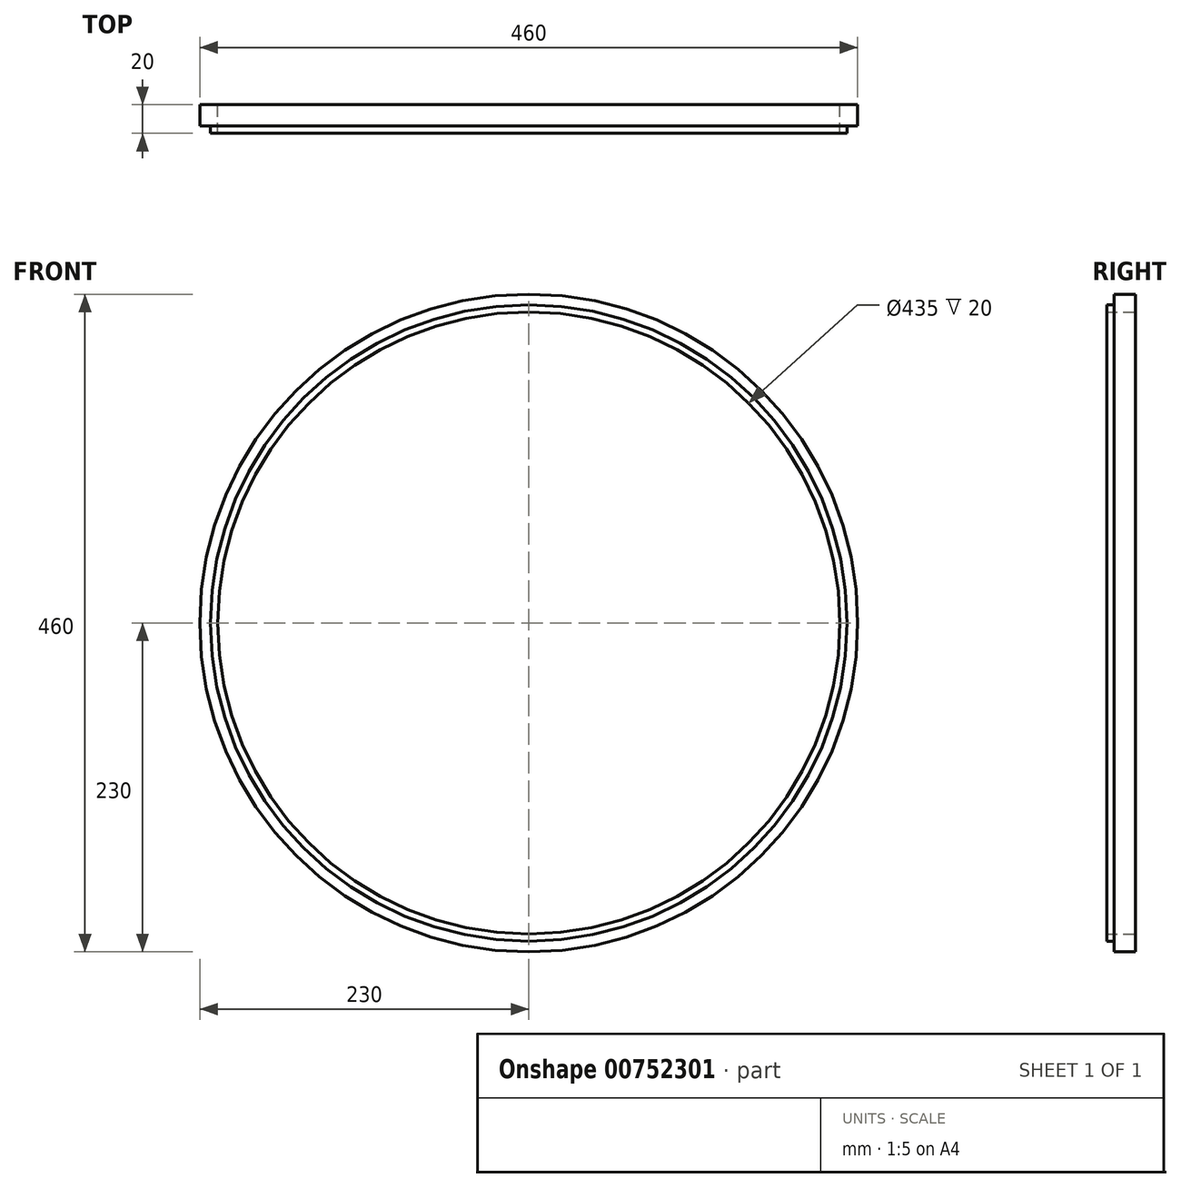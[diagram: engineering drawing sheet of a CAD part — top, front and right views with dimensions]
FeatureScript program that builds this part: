
annotation { "Feature Type Name" : "Feature", "Feature Type Description" : "" }
export const myFeature = defineFeature(function(context is Context, id is Id, definition is map)
    precondition{}
    {
        {
            var Q0;
            Q0=qCreatedBy(makeId("Front.planeOp"),FACE);
            var sketch = newSketch(context, id + "F0", { "sketchPlane" : qUnion([Q0])});
            skCircle(sketch, "E0", {"center": v(0, 0) * mm, "radius": 230 * mm});
            skCircle(sketch, "E1", {"center": v(0, 0) * mm, "radius": 217.5 * mm});
            skCircle(sketch, "E2", {"center": v(0, 0) * mm, "radius": 222.5 * mm});
            skSolve(sketch);
        }
        {
            var Q0;
            Q0=makeQuery(id+"F0.imprint","IMPRINT",FACE,{"disambiguationData":[TD([[makeQuery(id+"F0.imprint","IMPRINT",EDGE,{"derivedFrom":sQuery(id+"F0.wireOp",EDGE,"E1")}),-1.0]])]});
            extrude(context, id + "F1", {"entities" : qUnion([Q0]), "depth" : 20 * mm, "offsetDistance" : 25 * mm});
        }
        {
            var Q0;
            Q0=makeQuery(id+"F0.imprint","IMPRINT",FACE,{"disambiguationData":[TD([[makeQuery(id+"F0.imprint","IMPRINT",EDGE,{"derivedFrom":sQuery(id+"F0.wireOp",EDGE,"E0")}),1.0]])]});
            var Q1;
            Q1=sQuery(id+"F0.wireOp",EDGE,"E0");
            extrude(context, id + "F2", {"entities" : qUnion([Q0]), "operationType" : NewBodyOperationType.ADD, "surfaceEntities" : qUnion([Q1]), "depth" : 15 * mm, "offsetDistance" : 25 * mm});
        }
    });
